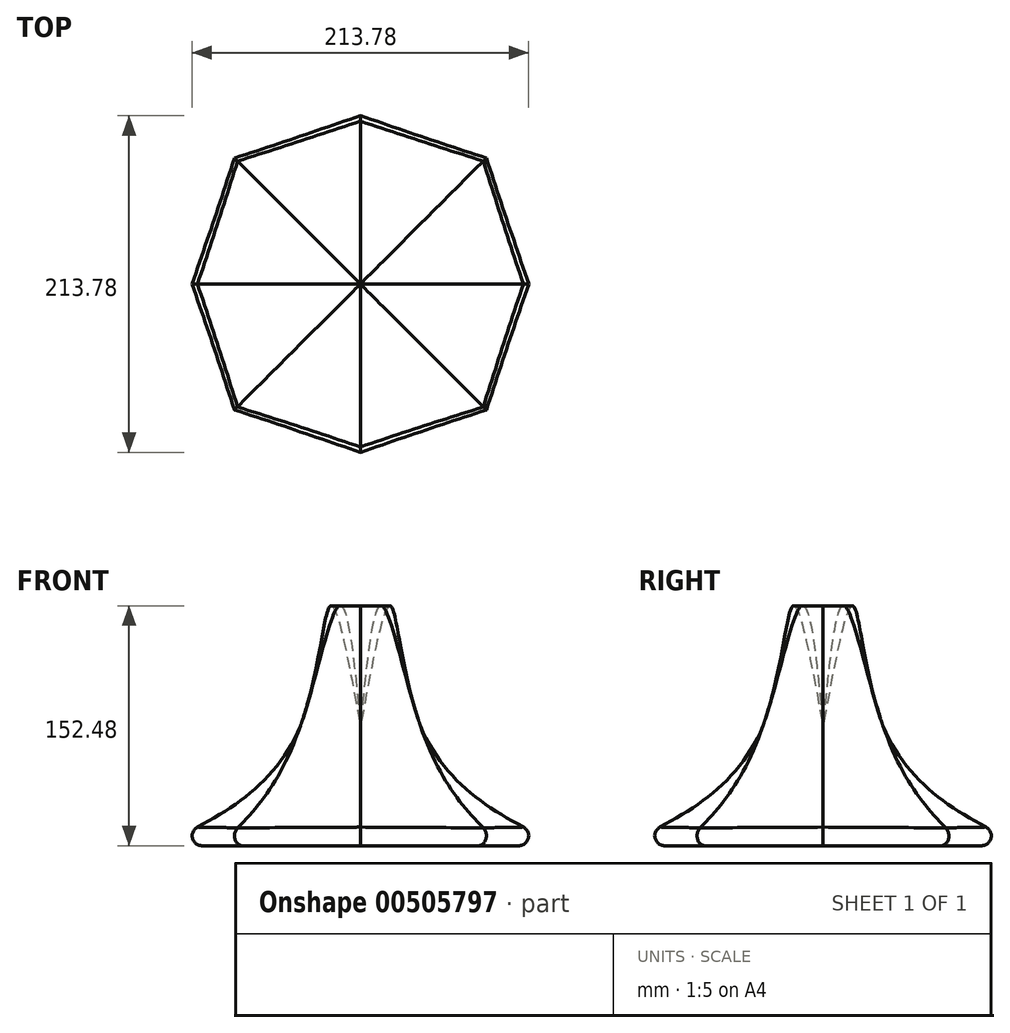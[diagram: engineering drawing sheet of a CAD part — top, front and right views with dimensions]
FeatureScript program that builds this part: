
annotation { "Feature Type Name" : "Feature", "Feature Type Description" : "" }
export const myFeature = defineFeature(function(context is Context, id is Id, definition is map)
    precondition{}
    {
        {
            var Q0;
            Q0=qCreatedBy(makeId("Top.planeOp"),FACE);
            var sketch = newSketch(context, id + "F0", { "sketchPlane" : qUnion([Q0])});
            skLineSegment(sketch, "E0.bottom", {"start": v(-38.1, 38.1) * mm, "end": v(0, 38.1) * mm});
            skLineSegment(sketch, "E0.top", {"start": v(-38.1, -38.1) * mm, "end": v(0, -38.1) * mm});
            skLineSegment(sketch, "E0.left", {"start": v(-38.1, 38.1) * mm, "end": v(-38.1, 0) * mm});
            skLineSegment(sketch, "E0.right", {"start": v(38.1, 38.1) * mm, "end": v(38.1, 0) * mm});
            skPoint(sketch, "E0.middle", {"position": v(0, 0) * mm});
            skLineSegment(sketch, "E1", {"start": v(0, 38.1) * mm, "end": v(38.1, 38.1) * mm});
            skLineSegment(sketch, "E2", {"start": v(-38.1, 0) * mm, "end": v(-38.1, -38.1) * mm});
            skLineSegment(sketch, "E3", {"start": v(38.1, 0) * mm, "end": v(38.1, -38.1) * mm});
            skLineSegment(sketch, "E4", {"start": v(0, -38.1) * mm, "end": v(38.1, -38.1) * mm});
            skSolve(sketch);
        }
        {
            var Q0;
            Q0=qCreatedBy(makeId("Top.planeOp"),FACE);
            cPlane(context, id + "F1", {"entities" : qUnion([Q0]), "cplaneType" : CPlaneType.OFFSET, "offset" : 76.2 * mm, "width" : 152.4 * mm, "height" : 152.4 * mm});
        }
        {
            var Q0;
            Q0=qCreatedBy(id+"F1.planeOp",FACE);
            var sketch = newSketch(context, id + "F2", { "sketchPlane" : qUnion([Q0])});
            skArc(sketch, "E5", {"start": v(0, 19.05) * mm, "mid": v(-7.3, 17.6) * mm, "end": v(-13.47, 13.47) * mm});
            skLineSegment(sketch, "E6", {"start": v(-13.47, 13.47) * mm, "end": v(-13.47, 13.47) * mm});
            skArc(sketch, "E7", {"start": v(-13.47, 13.47) * mm, "mid": v(-17.6, 7.3) * mm, "end": v(-19.05, 0) * mm});
            skLineSegment(sketch, "E8", {"start": v(-19.05, 0) * mm, "end": v(-19.05, 0) * mm});
            skArc(sketch, "E9", {"start": v(-19.05, 0) * mm, "mid": v(-17.6, -7.3) * mm, "end": v(-13.47, -13.47) * mm});
            skLineSegment(sketch, "E10", {"start": v(-13.47, -13.47) * mm, "end": v(-13.47, -13.47) * mm});
            skArc(sketch, "E11", {"start": v(-13.47, -13.47) * mm, "mid": v(-7.3, -17.6) * mm, "end": v(0, -19.05) * mm});
            skLineSegment(sketch, "E12", {"start": v(0, -19.05) * mm, "end": v(0, -19.05) * mm});
            skArc(sketch, "E13", {"start": v(0, -19.05) * mm, "mid": v(7.3, -17.6) * mm, "end": v(13.47, -13.47) * mm});
            skArc(sketch, "E14", {"start": v(13.47, -13.47) * mm, "mid": v(17.6, -7.3) * mm, "end": v(19.05, 0) * mm});
            skArc(sketch, "E15", {"start": v(19.05, 0) * mm, "mid": v(17.6, 7.3) * mm, "end": v(13.47, 13.47) * mm});
            skArc(sketch, "E16", {"start": v(13.47, 13.47) * mm, "mid": v(7.3, 17.6) * mm, "end": v(0, 19.05) * mm});
            skSolve(sketch);
        }
        {
            var Q0;
            Q0=qCreatedBy(makeId("Top.planeOp"),FACE);
            cPlane(context, id + "F3", {"entities" : qUnion([Q0]), "cplaneType" : CPlaneType.OFFSET, "offset" : 76.2 * mm, "oppositeDirection" : true, "width" : 152.4 * mm, "height" : 152.4 * mm});
        }
        {
            var Q0;
            Q0=qCreatedBy(id+"F3.planeOp",FACE);
            var sketch = newSketch(context, id + "F4", { "sketchPlane" : qUnion([Q0])});
            skCircle(sketch, "E17.cCircle", {"center": v(0, 0) * mm, "radius": 127 * mm, "construction": true});
            skLineSegment(sketch, "E17.0", {"start": v(127, 0) * mm, "end": v(89.8, -89.8) * mm});
            skLineSegment(sketch, "E17.1", {"start": v(89.8, -89.8) * mm, "end": v(0, -127) * mm});
            skLineSegment(sketch, "E17.2", {"start": v(0, -127) * mm, "end": v(-89.8, -89.8) * mm});
            skLineSegment(sketch, "E17.3", {"start": v(-89.8, -89.8) * mm, "end": v(-127, 0) * mm});
            skLineSegment(sketch, "E17.4", {"start": v(-127, 0) * mm, "end": v(-89.8, 89.8) * mm});
            skLineSegment(sketch, "E17.5", {"start": v(-89.8, 89.8) * mm, "end": v(0, 127) * mm});
            skLineSegment(sketch, "E17.6", {"start": v(0, 127) * mm, "end": v(89.8, 89.8) * mm});
            skLineSegment(sketch, "E17.7", {"start": v(89.8, 89.8) * mm, "end": v(127, 0) * mm});
            skSolve(sketch);
        }
        {
            var Q0;
            Q0=makeQuery(id+"F4.imprint","IMPRINT",FACE,{"disambiguationData":[TD([[makeQuery(id+"F4.imprint","IMPRINT",EDGE,{"derivedFrom":sQuery(id+"F4.wireOp",EDGE,"E17.0")}),-1.0]])]});
            var Q1;
            Q1=makeQuery(id+"F0.imprint","IMPRINT",FACE,{"disambiguationData":[TD([[makeQuery(id+"F0.imprint","IMPRINT",EDGE,{"derivedFrom":sQuery(id+"F0.wireOp",EDGE,"E0.bottom")}),-1.0]])]});
            var Q2;
            Q2=makeQuery(id+"F2.imprint","IMPRINT",FACE,{"disambiguationData":[TD([[makeQuery(id+"F2.imprint","IMPRINT",EDGE,{"derivedFrom":sQuery(id+"F2.wireOp",EDGE,"E5")}),1.0]])]});
            var Q3;
            Q3=sQuery(id+"F0.wireOp",VERTEX,"E0.middle");
            loft(context, id + "F5", {"sheetProfilesArray" : [{ "sheetProfileEntities" : qUnion([Q0]) }, { "sheetProfileEntities" : qUnion([Q1]) }, { "sheetProfileEntities" : qUnion([Q2]) }, { "sheetProfileEntities" : qUnion([Q3]) }]});
        }
        {
            var Q0;
            Q0=makeQuery(id+"F5.opLoft","MID_CAP_EDGE",EDGE,{"disambiguationData":[OSD([sQuery(id+"F4.wireOp",EDGE,"E17.2"),sQuery(id+"F4.wireOp",EDGE,"E17.3"),sQuery(id+"F4.wireOp",EDGE,"E17.4")])],"capPos":0.0});
            var Q1;
            Q1=makeQuery(id+"F5.opLoft","MID_CAP_EDGE",EDGE,{"disambiguationData":[OSD([sQuery(id+"F4.wireOp",EDGE,"E17.3"),sQuery(id+"F4.wireOp",EDGE,"E17.4"),sQuery(id+"F4.wireOp",EDGE,"E17.5")])],"capPos":0.0});
            var Q2;
            Q2=makeQuery(id+"F5.opLoft","MID_CAP_EDGE",EDGE,{"disambiguationData":[OSD([sQuery(id+"F4.wireOp",EDGE,"E17.4"),sQuery(id+"F4.wireOp",EDGE,"E17.5"),sQuery(id+"F4.wireOp",EDGE,"E17.6")])],"capPos":0.0});
            var Q3;
            Q3=makeQuery(id+"F5.opLoft","MID_CAP_EDGE",EDGE,{"disambiguationData":[OSD([sQuery(id+"F4.wireOp",EDGE,"E17.5"),sQuery(id+"F4.wireOp",EDGE,"E17.6"),sQuery(id+"F4.wireOp",EDGE,"E17.7")])],"capPos":0.0});
            var Q4;
            Q4=makeQuery(id+"F5.opLoft","MID_CAP_EDGE",EDGE,{"disambiguationData":[OSD([sQuery(id+"F4.wireOp",EDGE,"E17.0"),sQuery(id+"F4.wireOp",EDGE,"E17.6"),sQuery(id+"F4.wireOp",EDGE,"E17.7")])],"capPos":0.0});
            var Q5;
            Q5=makeQuery(id+"F5.opLoft","MID_CAP_EDGE",EDGE,{"disambiguationData":[OSD([sQuery(id+"F4.wireOp",EDGE,"E17.0"),sQuery(id+"F4.wireOp",EDGE,"E17.1"),sQuery(id+"F4.wireOp",EDGE,"E17.7")])],"capPos":0.0});
            var Q6;
            Q6=makeQuery(id+"F5.opLoft","MID_CAP_EDGE",EDGE,{"disambiguationData":[OSD([sQuery(id+"F4.wireOp",EDGE,"E17.0"),sQuery(id+"F4.wireOp",EDGE,"E17.1"),sQuery(id+"F4.wireOp",EDGE,"E17.2")])],"capPos":0.0});
            var Q7;
            Q7=makeQuery(id+"F5.opLoft","MID_CAP_EDGE",EDGE,{"disambiguationData":[OSD([sQuery(id+"F4.wireOp",EDGE,"E17.1"),sQuery(id+"F4.wireOp",EDGE,"E17.2"),sQuery(id+"F4.wireOp",EDGE,"E17.3")])],"capPos":0.0});
            fillet(context, id + "F6", {"entities" : qUnion([Q0, Q1, Q2, Q3, Q4, Q5, Q6, Q7]), "radius" : 6.35 * mm, "tangentPropagation" : true, "allowEdgeOverflow" : false});
        }
    });
